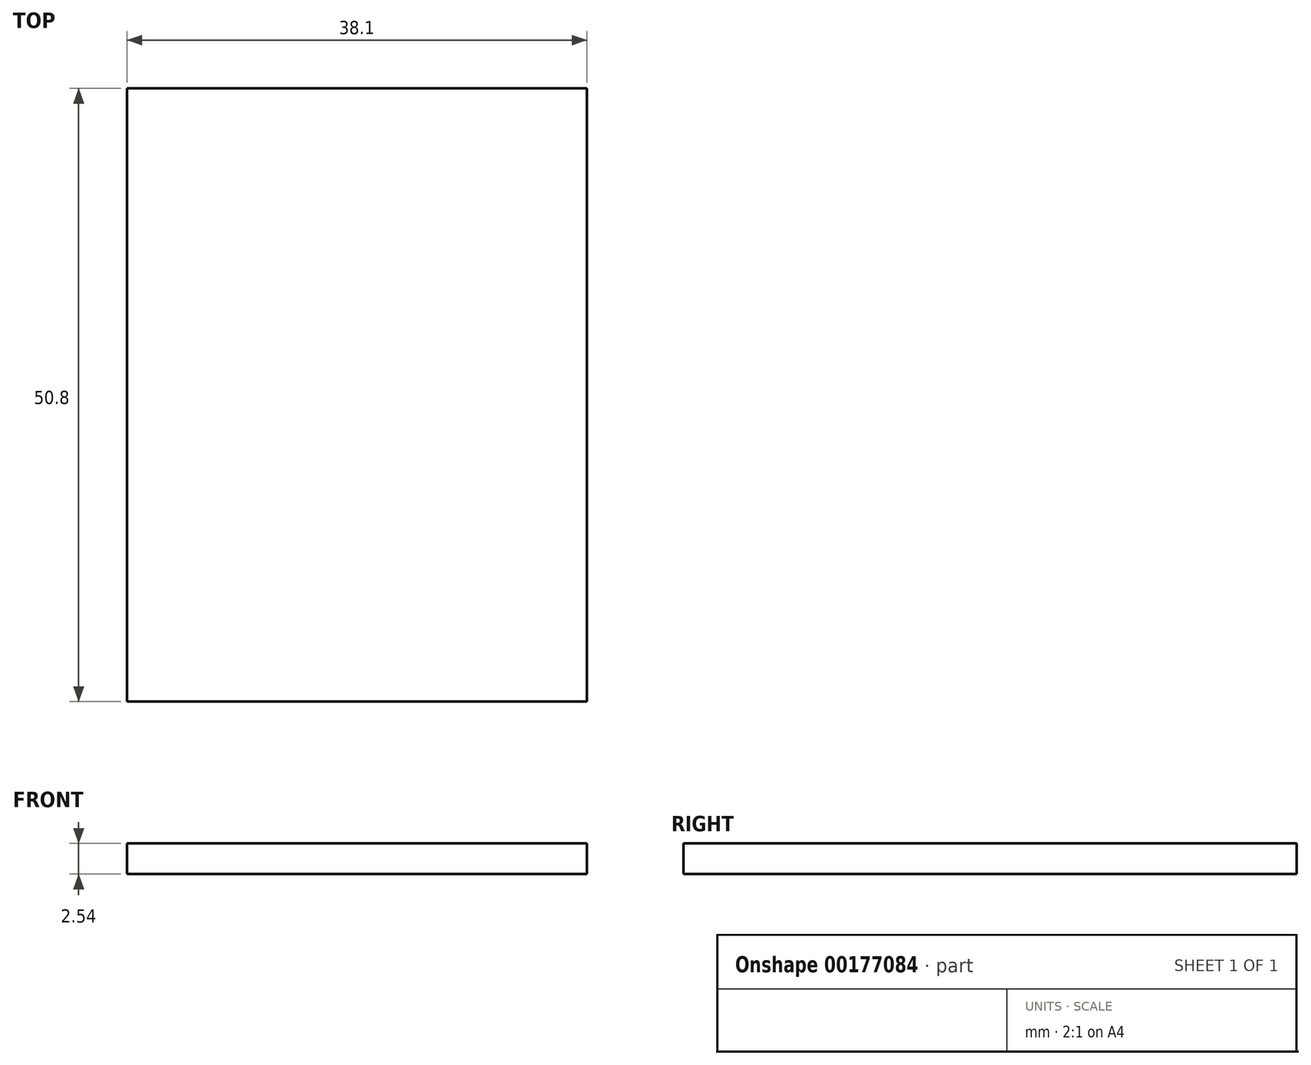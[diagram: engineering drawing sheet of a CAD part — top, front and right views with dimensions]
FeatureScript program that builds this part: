
annotation { "Feature Type Name" : "Feature", "Feature Type Description" : "" }
export const myFeature = defineFeature(function(context is Context, id is Id, definition is map)
    precondition{}
    {
        {
            var Q0;
            Q0=qCreatedBy(makeId("Front.planeOp"),FACE);
            var sketch = newSketch(context, id + "F0", { "sketchPlane" : qUnion([Q0])});
            skLineSegment(sketch, "E0.bottom", {"start": v(-19.05, 1.27) * mm, "end": v(19.05, 1.27) * mm});
            skLineSegment(sketch, "E0.top", {"start": v(-19.05, -1.27) * mm, "end": v(19.05, -1.27) * mm});
            skLineSegment(sketch, "E0.left", {"start": v(-19.05, 1.27) * mm, "end": v(-19.05, -1.27) * mm});
            skLineSegment(sketch, "E0.right", {"start": v(19.05, 1.27) * mm, "end": v(19.05, -1.27) * mm});
            skPoint(sketch, "E0.middle", {"position": v(0, 0) * mm});
            skSolve(sketch);
        }
        {
            var Q0;
            Q0=makeQuery(id+"F0.imprint","IMPRINT",FACE,{"disambiguationData":[TD([[makeQuery(id+"F0.imprint","IMPRINT",EDGE,{"derivedFrom":sQuery(id+"F0.wireOp",EDGE,"E0.bottom")}),-1.0]])]});
            extrude(context, id + "F1", {"entities" : qUnion([Q0]), "depth" : 50.8 * mm});
        }
    });
